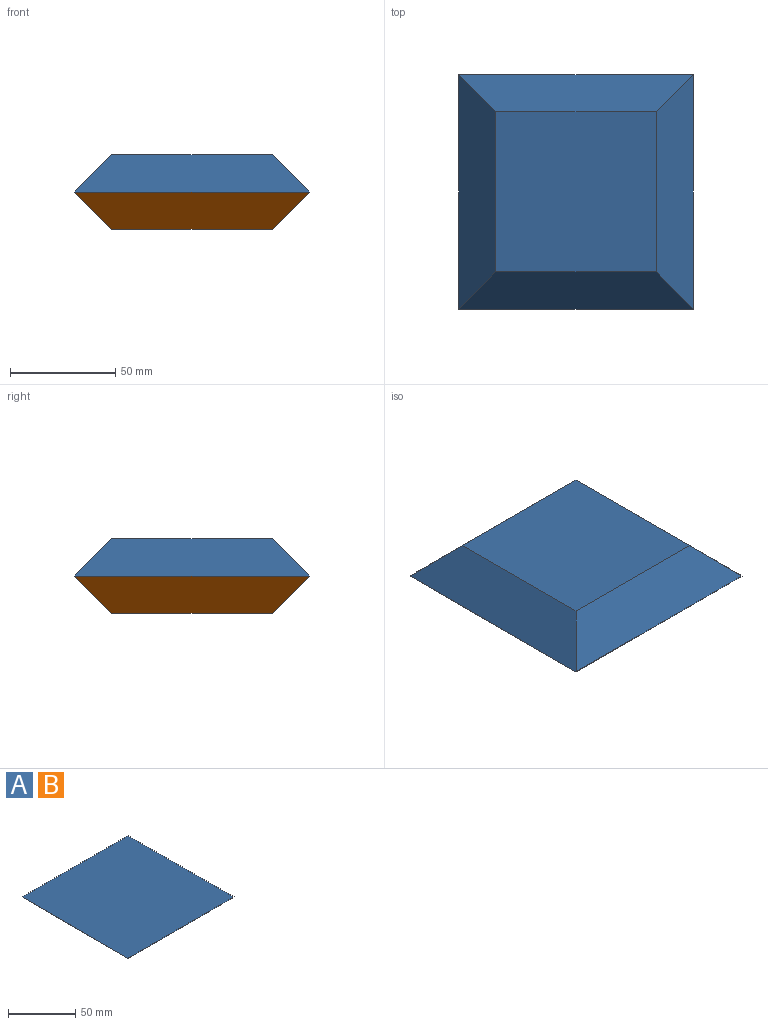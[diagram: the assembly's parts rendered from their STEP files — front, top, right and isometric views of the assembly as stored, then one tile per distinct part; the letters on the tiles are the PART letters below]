
ASSEMBLY  parts=2 mates=1
PART A: 6 faces, bbox 111.8x111.8x17.8 mm
  f0: plane 111.76x17.78mm, normal (0,0.71,-0.71), area 2363.1mm2, adj f1,f3,f4,f5
  f1: plane 111.76x17.78mm, normal (-0.71,0,-0.71), area 2363.1mm2, adj f0,f2,f4,f5
  f2: plane 111.76x17.78mm, normal (0,-0.71,-0.71), area 2363.1mm2, adj f1,f3,f4,f5
  f3: plane 111.76x17.78mm, normal (0.71,0,-0.71), area 2363.1mm2, adj f0,f2,f4,f5
  f4: plane 111.76x111.76mm, normal (0,0,1), area 12490.3mm2, adj f0,f1,f2,f3
  f5: plane 76.2x76.2mm, normal (0,0,-1), area 5806.4mm2, adj f0,f1,f2,f3
PART B: same geometry as A
PLACE A rot(axis=(1,0,0),180deg) t=(-7.47,4.71,28.76)mm
PLACE B t=(-7.47,4.71,-6.8)mm
MATE fastened A.f4 <-> B.f4  axis (0,0,-1) through (-7.47,4.71,10.98)mm
